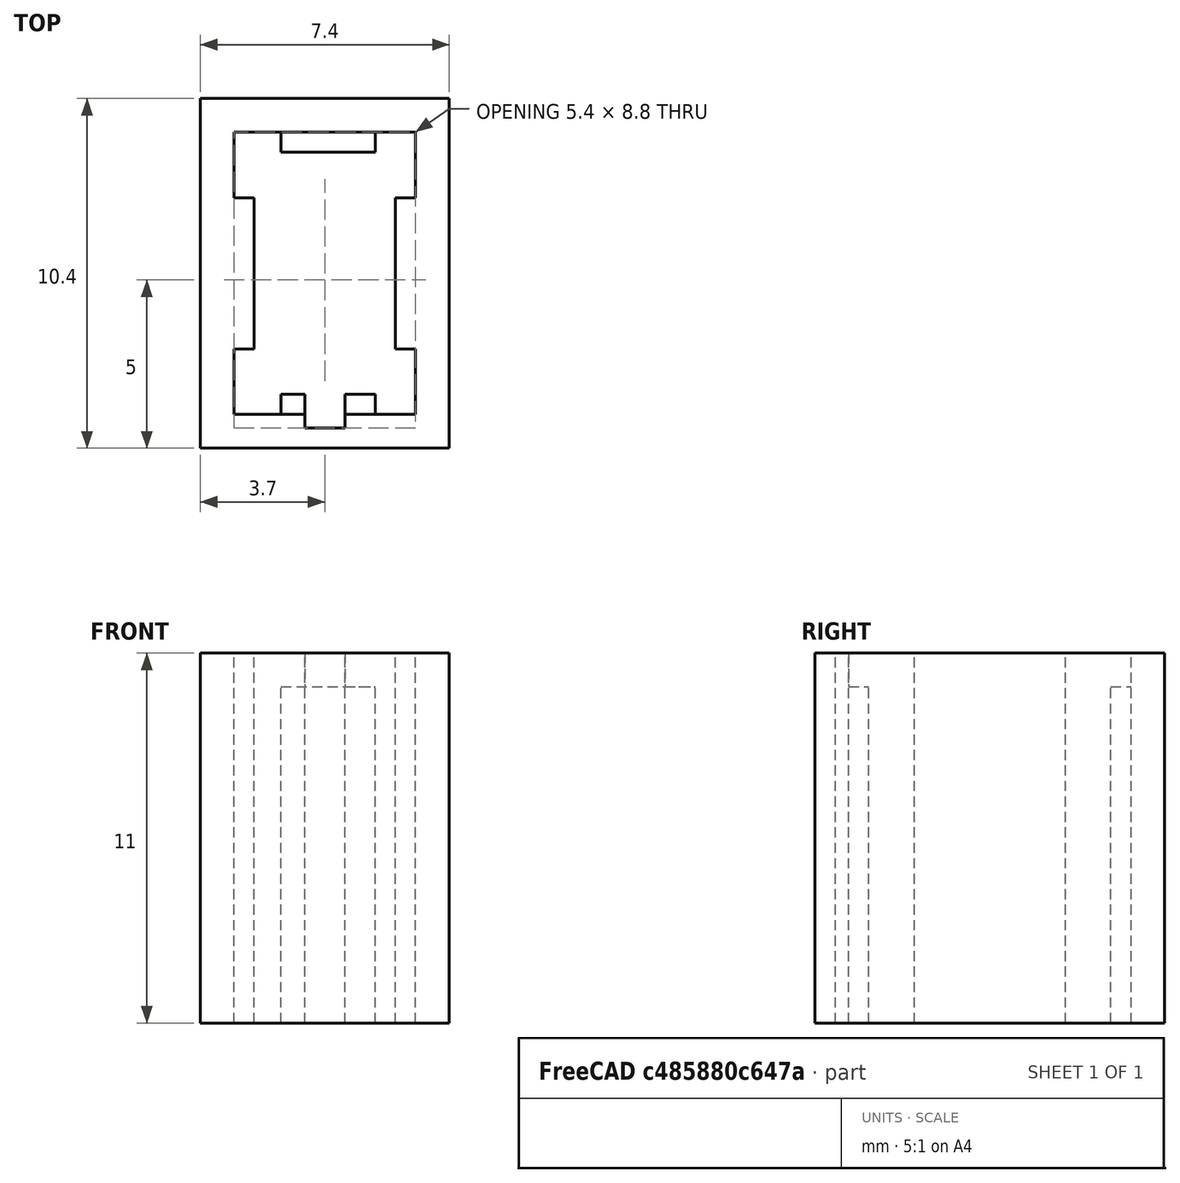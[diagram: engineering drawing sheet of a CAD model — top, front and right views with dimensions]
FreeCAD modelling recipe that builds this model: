
FCSTD DOCUMENT  (FreeCAD 0.18R16146 (Git))
Label: microfit-stack
License: All rights reserved
LicenseURL: http://en.wikipedia.org/wiki/All_rights_reserved
objects: Part::Box×7, Part::Cut×2, Part::MultiFuse×1
note: 10 computed .brp shape members not serialized (recipe doc carries the construction recipe); baked Part::Feature solids carry a one-line shape summary decoded from their .brp

FEATURE [Part::Box] Box  label="Cube"
  AttacherType = Attacher::AttachEngine3D
  Height = 11
  Length = 0.6
  Placement = pos=(0,1.95,0) rot=(0,0,1;0rad)
  Width = 4.5
FEATURE [Part::Box] Box001  label="Cube001"
  AttacherType = Attacher::AttachEngine3D
  Height = 11
  Length = 7.4
  Placement = pos=(-1,-1,0) rot=(0,0,1;0rad)
  Width = 10.4
FEATURE [Part::Box] Box002  label="Cube002"
  AttacherType = Attacher::AttachEngine3D
  Height = 11
  Length = 5.4
  Width = 8.4
FEATURE [Part::Cut] Cut
  Base = -> Box001
  Tool = -> Box002
FEATURE [Part::Box] Box003  label="Cube003"
  AttacherType = Attacher::AttachEngine3D
  Height = 11
  Length = 0.6
  Placement = pos=(4.8,1.95,0) rot=(0,0,1;0rad)
  Width = 4.5
FEATURE [Part::Box] Box004  label="Cube004"
  AttacherType = Attacher::AttachEngine3D
  Height = 10
  Length = 2.8
  Placement = pos=(1.4,0,0) rot=(0,0,1;0rad)
  Width = 0.6
FEATURE [Part::Box] Box005  label="Cube005"
  AttacherType = Attacher::AttachEngine3D
  Height = 10
  Length = 2.8
  Placement = pos=(1.4,7.8,0) rot=(0,0,1;0rad)
  Width = 0.6
FEATURE [Part::Box] Box006  label="Cube006"
  AttacherType = Attacher::AttachEngine3D
  Height = 11
  Length = 1.2
  Placement = pos=(2.1,-0.4,0) rot=(0,0,1;0rad)
  Width = 1
FEATURE [Part::MultiFuse] Fusion
  Shapes = -> [Box,Cut,Box003,Box004,Box005]
FEATURE [Part::Cut] Cut001
  Base = -> Fusion
  Tool = -> Box006
